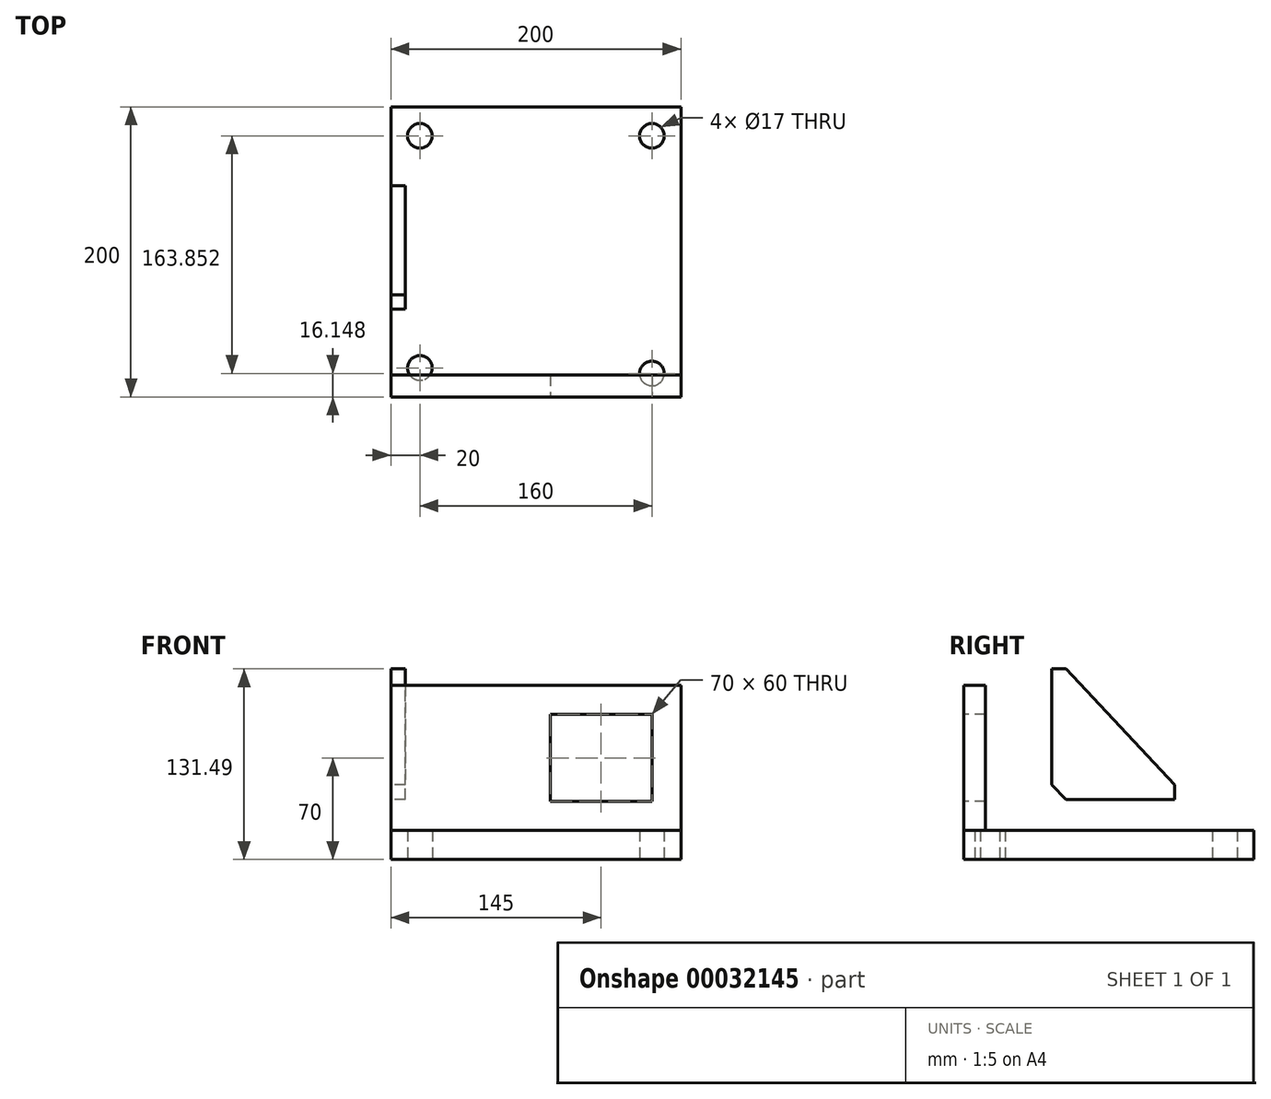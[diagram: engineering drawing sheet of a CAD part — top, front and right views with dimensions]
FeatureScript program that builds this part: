
annotation { "Feature Type Name" : "Feature", "Feature Type Description" : "" }
export const myFeature = defineFeature(function(context is Context, id is Id, definition is map)
    precondition{}
    {
        {
            var Q0;
            Q0=qCreatedBy(makeId("Top.planeOp"),FACE);
            var sketch = newSketch(context, id + "F0", { "sketchPlane" : qUnion([Q0])});
            skLineSegment(sketch, "E0.bottom", {"start": v(0, 0) * mm, "end": v(200, 0) * mm});
            skLineSegment(sketch, "E0.top", {"start": v(0, 200) * mm, "end": v(200, 200) * mm});
            skLineSegment(sketch, "E0.left", {"start": v(0, 0) * mm, "end": v(0, 200) * mm});
            skLineSegment(sketch, "E0.right", {"start": v(200, 0) * mm, "end": v(200, 200) * mm});
            skCircle(sketch, "E1", {"center": v(20, 180) * mm, "radius": 8.5 * mm});
            skCircle(sketch, "E2", {"center": v(180, 180) * mm, "radius": 8.5 * mm});
            skCircle(sketch, "E3", {"center": v(180, 16.15) * mm, "radius": 8.5 * mm});
            skCircle(sketch, "E4", {"center": v(20, 20) * mm, "radius": 8.5 * mm});
            skSolve(sketch);
        }
        {
            var Q0;
            Q0 = qSketchRegion(id + "F0", true);
            extrude(context, id + "F1", {"entities" : qUnion([Q0]), "depth" : 20 * mm});
        }
        {
            var Q0;
            Q0=qCreatedBy(makeId("Front.planeOp"),FACE);
            var sketch = newSketch(context, id + "F2", { "sketchPlane" : qUnion([Q0])});
            skLineSegment(sketch, "E5.bottom", {"start": v(0, 20) * mm, "end": v(200, 20) * mm});
            skLineSegment(sketch, "E5.top", {"start": v(0, 120) * mm, "end": v(200, 120) * mm});
            skLineSegment(sketch, "E5.left", {"start": v(0, 20) * mm, "end": v(0, 120) * mm});
            skLineSegment(sketch, "E5.right", {"start": v(200, 20) * mm, "end": v(200, 120) * mm});
            skSolve(sketch);
        }
        {
            var Q0;
            Q0 = qSketchRegion(id + "F2", true);
            extrude(context, id + "F3", {"entities" : qUnion([Q0]), "oppositeDirection" : true, "depth" : 15 * mm});
        }
        {
            var Q0;
            Q0=qCreatedBy(makeId("Right.planeOp"),FACE);
            var sketch = newSketch(context, id + "F4", { "sketchPlane" : qUnion([Q0])});
            skLineSegment(sketch, "E6", {"start": v(60.5, 131.5) * mm, "end": v(70.5, 131.5) * mm});
            skLineSegment(sketch, "E7", {"start": v(70.5, 131.5) * mm, "end": v(145.5, 51.5) * mm});
            skLineSegment(sketch, "E8", {"start": v(145.5, 51.5) * mm, "end": v(145.5, 41.5) * mm});
            skLineSegment(sketch, "E9", {"start": v(145.5, 41.5) * mm, "end": v(70.5, 41.5) * mm});
            skLineSegment(sketch, "E10", {"start": v(70.5, 41.5) * mm, "end": v(60.5, 51.5) * mm});
            skLineSegment(sketch, "E11", {"start": v(60.5, 51.5) * mm, "end": v(60.5, 131.5) * mm});
            skSolve(sketch);
        }
        {
            var Q0;
            Q0 = qSketchRegion(id + "F4", true);
            extrude(context, id + "F5", {"entities" : qUnion([Q0]), "depth" : 10 * mm});
        }
        {
            var Q0;
            Q0=qCreatedBy(makeId("Front.planeOp"),FACE);
            var sketch = newSketch(context, id + "F6", { "sketchPlane" : qUnion([Q0])});
            skLineSegment(sketch, "E12.bottom", {"start": v(110, 100) * mm, "end": v(180, 100) * mm});
            skLineSegment(sketch, "E12.top", {"start": v(110, 40) * mm, "end": v(180, 40) * mm});
            skLineSegment(sketch, "E12.left", {"start": v(110, 100) * mm, "end": v(110, 40) * mm});
            skLineSegment(sketch, "E12.right", {"start": v(180, 100) * mm, "end": v(180, 40) * mm});
            skSolve(sketch);
        }
        {
            var Q0;
            Q0=makeQuery(id+"F6.imprint","IMPRINT",FACE,{"disambiguationData":[TD([[makeQuery(id+"F6.imprint","IMPRINT",EDGE,{"derivedFrom":sQuery(id+"F6.wireOp",EDGE,"E12.bottom")}),-1.0]])]});
            extrude(context, id + "F7", {"entities" : qUnion([Q0]), "operationType" : NewBodyOperationType.REMOVE, "endBound" : BoundingType.THROUGH_ALL, "oppositeDirection" : true, "depth" : 15 * mm, "offsetDistance" : 25 * mm});
        }
    });
